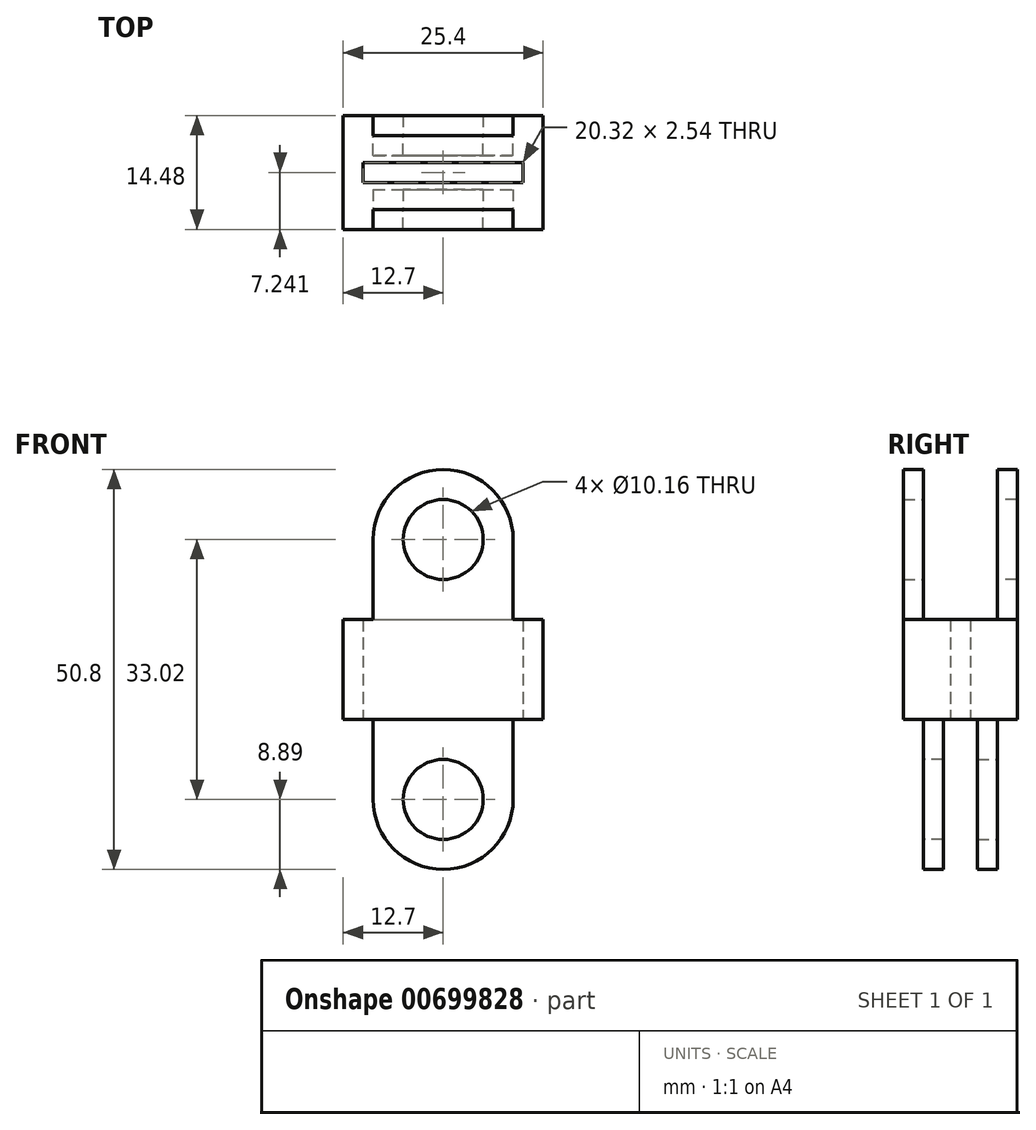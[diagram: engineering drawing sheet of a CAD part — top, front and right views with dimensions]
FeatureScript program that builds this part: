
annotation { "Feature Type Name" : "Feature", "Feature Type Description" : "" }
export const myFeature = defineFeature(function(context is Context, id is Id, definition is map)
    precondition{}
    {
        {
            var Q0;
            Q0=qCreatedBy(makeId("Front.planeOp"),FACE);
            var sketch = newSketch(context, id + "F0", { "sketchPlane" : qUnion([Q0])});
            skLineSegment(sketch, "E0.bottom", {"start": v(0, 0) * mm, "end": v(25.4, 0) * mm});
            skLineSegment(sketch, "E0.top", {"start": v(0, 12.7) * mm, "end": v(25.4, 12.7) * mm});
            skLineSegment(sketch, "E0.left", {"start": v(0, 0) * mm, "end": v(0, 12.7) * mm});
            skLineSegment(sketch, "E0.right", {"start": v(25.4, 0) * mm, "end": v(25.4, 12.7) * mm});
            skLineSegment(sketch, "E1", {"start": v(1.27, 2.54) * mm, "end": v(1.27, 3.8) * mm});
            skLineSegment(sketch, "E2", {"start": v(1.27, 12.7) * mm, "end": v(24.13, 12.7) * mm});
            skLineSegment(sketch, "E3", {"start": v(24.13, 10.16) * mm, "end": v(24.13, 8.9) * mm});
            skLineSegment(sketch, "E4", {"start": v(0.64, 3.17) * mm, "end": v(1.9, 3.17) * mm});
            skLineSegment(sketch, "E5", {"start": v(25.4, 3.18) * mm, "end": v(25.4, 6.35) * mm});
            skLineSegment(sketch, "E6", {"start": v(24.77, 6.35) * mm, "end": v(23.5, 6.35) * mm});
            skLineSegment(sketch, "E7", {"start": v(0, 6.35) * mm, "end": v(0, 9.52) * mm});
            skLineSegment(sketch, "E8", {"start": v(0.64, 9.52) * mm, "end": v(1.9, 9.52) * mm});
            skPoint(sketch, "E9.orphan", {"position": v(25.4, 9.53) * mm});
            skLineSegment(sketch, "E10.trimOffspring", {"start": v(24.13, 6.99) * mm, "end": v(24.13, 5.72) * mm});
            skLineSegment(sketch, "E11.trimOffspring", {"start": v(23.5, 9.53) * mm, "end": v(24.77, 9.53) * mm});
            skLineSegment(sketch, "E12.trimOffspring", {"start": v(1.9, 6.35) * mm, "end": v(0.64, 6.35) * mm});
            skLineSegment(sketch, "E13.trimOffspring", {"start": v(24.13, 3.81) * mm, "end": v(24.13, 2.54) * mm});
            skLineSegment(sketch, "E14.trimOffspring", {"start": v(23.5, 3.18) * mm, "end": v(24.77, 3.18) * mm});
            skPoint(sketch, "E15.orphan", {"position": v(24.13, 0) * mm});
            skLineSegment(sketch, "E16.trimOffspring", {"start": v(1.27, 5.71) * mm, "end": v(1.27, 6.98) * mm});
            skLineSegment(sketch, "E17.trimOffspring", {"start": v(1.27, 8.89) * mm, "end": v(1.27, 10.16) * mm});
            skSolve(sketch);
        }
        {
            var Q0;
            Q0=makeQuery(id+"F0.imprint","IMPRINT",FACE,{"disambiguationData":[TD([[makeQuery(id+"F0.imprint","IMPRINT",EDGE,{"derivedFrom":sQuery(id+"F0.wireOp",EDGE,"E0.bottom")}),1.0]])]});
            extrude(context, id + "F1", {"entities" : qUnion([Q0]), "depth" : 9.4 * mm});
        }
        {
            var Q0;
            Q0=makeQuery(id+"F1.opExtrude","CAP_FACE",FACE,{"disambiguationData":[OSD([sQuery(id+"F0.wireOp",EDGE,"E0.bottom"),sQuery(id+"F0.wireOp",EDGE,"E0.top"),sQuery(id+"F0.wireOp",EDGE,"E0.left"),sQuery(id+"F0.wireOp",EDGE,"E0.right"),sQuery(id+"F0.wireOp",EDGE,"E2"),sQuery(id+"F0.wireOp",EDGE,"E5"),sQuery(id+"F0.wireOp",EDGE,"E7")])],"isStart":false});
            var sketch = newSketch(context, id + "F2", { "sketchPlane" : qUnion([Q0])});
            skLineSegment(sketch, "E18.bottom", {"start": v(3.81, 12.7) * mm, "end": v(21.59, 12.7) * mm});
            skLineSegment(sketch, "E18.top", {"start": v(3.81, 22.86) * mm, "end": v(21.59, 22.86) * mm});
            skLineSegment(sketch, "E18.left", {"start": v(3.81, 12.7) * mm, "end": v(3.81, 22.86) * mm});
            skLineSegment(sketch, "E18.right", {"start": v(21.59, 12.7) * mm, "end": v(21.59, 22.86) * mm});
            skLineSegment(sketch, "E19", {"start": v(12.7, 17.78) * mm, "end": v(12.7, 22.86) * mm});
            skArc(sketch, "E20", {"start": v(21.59, 22.86) * mm, "mid": v(12.7, 31.75) * mm, "end": v(3.81, 22.86) * mm});
            skCircle(sketch, "E21", {"center": v(12.7, 22.86) * mm, "radius": 5.08 * mm});
            skPoint(sketch, "E22.orphan", {"position": v(12.7, 12.7) * mm});
            skLineSegment(sketch, "E23", {"start": v(0, 6.35) * mm, "end": v(25.4, 6.35) * mm});
            skLineSegment(sketch, "E24.MirrorCS", {"start": v(21.59, 0) * mm, "end": v(21.59, -10.16) * mm});
            skLineSegment(sketch, "E25.MirrorCS", {"start": v(3.81, 0) * mm, "end": v(3.81, -10.16) * mm});
            skArc(sketch, "E26.MirrorCS", {"start": v(21.59, -10.16) * mm, "mid": v(12.7, -19.05) * mm, "end": v(3.81, -10.16) * mm});
            skCircle(sketch, "E27.MirrorC", {"center": v(12.7, -10.16) * mm, "radius": 5.08 * mm});
            skSolve(sketch);
        }
        {
            var Q0;
            Q0=makeQuery(id+"F1.opExtrude","CAP_FACE",FACE,{"disambiguationData":[OSD([sQuery(id+"F0.wireOp",EDGE,"E0.bottom"),sQuery(id+"F0.wireOp",EDGE,"E0.top"),sQuery(id+"F0.wireOp",EDGE,"E0.left"),sQuery(id+"F0.wireOp",EDGE,"E0.right"),sQuery(id+"F0.wireOp",EDGE,"E2"),sQuery(id+"F0.wireOp",EDGE,"E5"),sQuery(id+"F0.wireOp",EDGE,"E7")])],"isStart":true});
            var sketch = newSketch(context, id + "F3", { "sketchPlane" : qUnion([Q0])});
            skLineSegment(sketch, "E28.bottom", {"start": v(-21.59, 12.7) * mm, "end": v(-3.81, 12.7) * mm});
            skLineSegment(sketch, "E28.top", {"start": v(-21.59, 22.86) * mm, "end": v(-3.81, 22.86) * mm});
            skLineSegment(sketch, "E28.left", {"start": v(-21.59, 12.7) * mm, "end": v(-21.59, 22.86) * mm});
            skLineSegment(sketch, "E28.right", {"start": v(-3.81, 12.7) * mm, "end": v(-3.81, 22.86) * mm});
            skLineSegment(sketch, "E29", {"start": v(-12.7, 17.78) * mm, "end": v(-12.7, 22.86) * mm});
            skCircle(sketch, "E30", {"center": v(-12.7, 22.86) * mm, "radius": 5.08 * mm});
            skArc(sketch, "E31", {"start": v(-3.81, 22.86) * mm, "mid": v(-12.7, 31.75) * mm, "end": v(-21.6, 22.86) * mm});
            skLineSegment(sketch, "E32", {"start": v(-25.4, 6.35) * mm, "end": v(0, 6.35) * mm});
            skLineSegment(sketch, "E33.MirrorCS", {"start": v(-21.59, 0) * mm, "end": v(-21.59, -10.16) * mm});
            skLineSegment(sketch, "E34.MirrorCS", {"start": v(-3.81, 0) * mm, "end": v(-3.81, -10.16) * mm});
            skCircle(sketch, "E35.MirrorC", {"center": v(-12.7, -10.16) * mm, "radius": 5.08 * mm});
            skArc(sketch, "E36.MirrorC", {"start": v(-3.81, -10.16) * mm, "mid": v(-12.7, -19.05) * mm, "end": v(-21.6, -10.16) * mm});
            skPoint(sketch, "E37.orphan", {"position": v(-12.7, 12.7) * mm});
            skSolve(sketch);
        }
        {
            var Q0;
            {var subQ3=sQuery(id+"F3.wireOp",EDGE,"E28.bottom");Q0=makeQuery(id+"F3.imprint","IMPRINT",FACE,{"disambiguationData":[TD([[makeQuery(id+"F3.imprint","IMPRINT",EDGE,{"derivedFrom":subQ3}),1.0]])]});}
            var Q1;
            {var subQ7=sQuery(id+"F3.wireOp",EDGE,"E32");Q1=makeQuery(id+"F3.imprint","IMPRINT",FACE,{"disambiguationData":[TD([[makeQuery(id+"F3.imprint","IMPRINT",EDGE,{"derivedFrom":subQ7}),-1.0]])]});}
            var Q2;
            {var subQ0=sQuery(id+"F3.wireOp",EDGE,"E31");Q2=makeQuery(id+"F3.imprint","IMPRINT",FACE,{"disambiguationData":[TD([[makeQuery(id+"F3.imprint","IMPRINT",EDGE,{"derivedFrom":subQ0}),1.0]])]});}
            var Q3;
            Q3=makeQuery(id+"F3.imprint","IMPRINT",FACE,{"disambiguationData":[TD([[makeQuery(id+"F3.imprint","IMPRINT",EDGE,{"derivedFrom":sQuery(id+"F3.wireOp",EDGE,"E28.bottom")}),-1.0]])]});
            var Q4;
            {var subQ1=sQuery(id+"F2.wireOp",EDGE,"E24.MirrorCS");Q4=makeQuery(id+"F2.imprint","IMPRINT",FACE,{"disambiguationData":[TD([[makeQuery(id+"F2.imprint","IMPRINT",EDGE,{"derivedFrom":subQ1}),-1.0]])]});}
            extrude(context, id + "F4", {"entities" : qUnion([Q0, Q1, Q2, Q3, Q4]), "operationType" : NewBodyOperationType.ADD, "depth" : 2.54 * mm});
        }
        {
            var Q0;
            {var subQ1=sQuery(id+"F3.wireOp",EDGE,"E33.MirrorCS");Q0=makeQuery(id+"F3.imprint","IMPRINT",FACE,{"disambiguationData":[TD([[makeQuery(id+"F3.imprint","IMPRINT",EDGE,{"derivedFrom":subQ1}),1.0]])]});}
            var Q1;
            Q1=makeQuery(id+"F2.imprint","IMPRINT",FACE,{"disambiguationData":[TD([[makeQuery(id+"F2.imprint","IMPRINT",EDGE,{"derivedFrom":sQuery(id+"F2.wireOp",EDGE,"E18.bottom")}),1.0]])]});
            var Q2;
            {var subQ0=sQuery(id+"F2.wireOp",EDGE,"E20");Q2=makeQuery(id+"F2.imprint","IMPRINT",FACE,{"disambiguationData":[TD([[makeQuery(id+"F2.imprint","IMPRINT",EDGE,{"derivedFrom":subQ0}),1.0]])]});}
            var Q3;
            {var subQ3=sQuery(id+"F2.wireOp",EDGE,"E18.bottom");Q3=makeQuery(id+"F2.imprint","IMPRINT",FACE,{"disambiguationData":[TD([[makeQuery(id+"F2.imprint","IMPRINT",EDGE,{"derivedFrom":subQ3}),-1.0]])]});}
            var Q4;
            {var subQ7=sQuery(id+"F2.wireOp",EDGE,"E23");Q4=makeQuery(id+"F2.imprint","IMPRINT",FACE,{"disambiguationData":[TD([[makeQuery(id+"F2.imprint","IMPRINT",EDGE,{"derivedFrom":subQ7}),-1.0]])]});}
            extrude(context, id + "F5", {"entities" : qUnion([Q0, Q1, Q2, Q3, Q4]), "operationType" : NewBodyOperationType.ADD, "depth" : -2.54 * mm});
        }
        {
            var Q0;
            {var subQ0=sQuery(id+"F0.wireOp",EDGE,"E0.bottom");var subQ1=makeQuery(id+"F1.opExtrude","CAP_EDGE",EDGE,{"disambiguationData":[OSD([subQ0])],"isStart":false});var subQ2=makeQuery(id+"F2.imprint","INTERSECT",VERTEX,{"derivedFrom":[subQ1,sQuery(id+"F2.wireOp",EDGE,"E24.MirrorCS")]});var subQ3=makeQuery(id+"F2.imprint","INTERSECT",VERTEX,{"derivedFrom":[subQ1,sQuery(id+"F2.wireOp",EDGE,"E25.MirrorCS")]});var subQ8=makeQuery(id+"F1.opExtrude","CAP_EDGE",EDGE,{"disambiguationData":[OSD([subQ0])],"isStart":true});var subQ9=makeQuery(id+"F3.imprint","INTERSECT",VERTEX,{"derivedFrom":[subQ8,sQuery(id+"F3.wireOp",EDGE,"E33.MirrorCS")]});var subQ10=makeQuery(id+"F3.imprint","INTERSECT",VERTEX,{"derivedFrom":[subQ8,sQuery(id+"F3.wireOp",EDGE,"E34.MirrorCS")]});Q0=makeQuery(id+"F5.boolean.opBoolean","MERGE",FACE,{"derivedFrom":[makeQuery(id+"F4.boolean.opBoolean","MERGE",FACE,{"derivedFrom":[makeQuery(id+"F1.opExtrude","SWEPT_FACE",FACE,{"disambiguationData":[OSD([subQ0])]}),makeQuery(id+"F4.opExtrude","SWEPT_FACE",FACE,{"disambiguationData":[OSD([subQ0]),TDD([makeQuery(id+"F3.imprint","IMPRINT",EDGE,{"disambiguationData":[TD([[subQ10,1.0]])],"derivedFrom":subQ8}),makeQuery(id+"F3.imprint","IMPRINT",EDGE,{"disambiguationData":[TD([[subQ9,-1.0]])],"derivedFrom":subQ8}),makeQuery(id+"F3.imprint","IMPRINT",EDGE,{"disambiguationData":[TD([[subQ9,1.0]])],"derivedFrom":subQ8})])]})]}),makeQuery(id+"F5.opExtrude","SWEPT_FACE",FACE,{"disambiguationData":[OSD([subQ0]),TDD([makeQuery(id+"F2.imprint","IMPRINT",EDGE,{"disambiguationData":[TD([[subQ3,1.0]])],"derivedFrom":subQ1}),makeQuery(id+"F2.imprint","IMPRINT",EDGE,{"disambiguationData":[TD([[subQ2,-1.0]])],"derivedFrom":subQ1}),makeQuery(id+"F2.imprint","IMPRINT",EDGE,{"disambiguationData":[TD([[subQ2,1.0]])],"derivedFrom":subQ1})])]})]});}
            var sketch = newSketch(context, id + "F6", { "sketchPlane" : qUnion([Q0])});
            skLineSegment(sketch, "E38", {"start": v(21.59, 6.86) * mm, "end": v(3.81, 2.54) * mm});
            skLineSegment(sketch, "E39.bottom", {"start": v(22.86, 3.43) * mm, "end": v(2.54, 3.43) * mm});
            skLineSegment(sketch, "E39.top", {"start": v(22.86, 5.97) * mm, "end": v(2.54, 5.97) * mm});
            skLineSegment(sketch, "E39.left", {"start": v(22.86, 3.43) * mm, "end": v(22.86, 5.97) * mm});
            skLineSegment(sketch, "E39.right", {"start": v(2.54, 3.43) * mm, "end": v(2.54, 5.97) * mm});
            skPoint(sketch, "E39.middle", {"position": v(12.7, 4.7) * mm});
            skSolve(sketch);
        }
        {
            var Q0;
            Q0=qSketchRegion(id+"F6",true);
            extrude(context, id + "F7", {"entities" : qUnion([Q0]), "operationType" : NewBodyOperationType.REMOVE, "oppositeDirection" : true, "depth" : 25.4 * mm});
        }
    });
